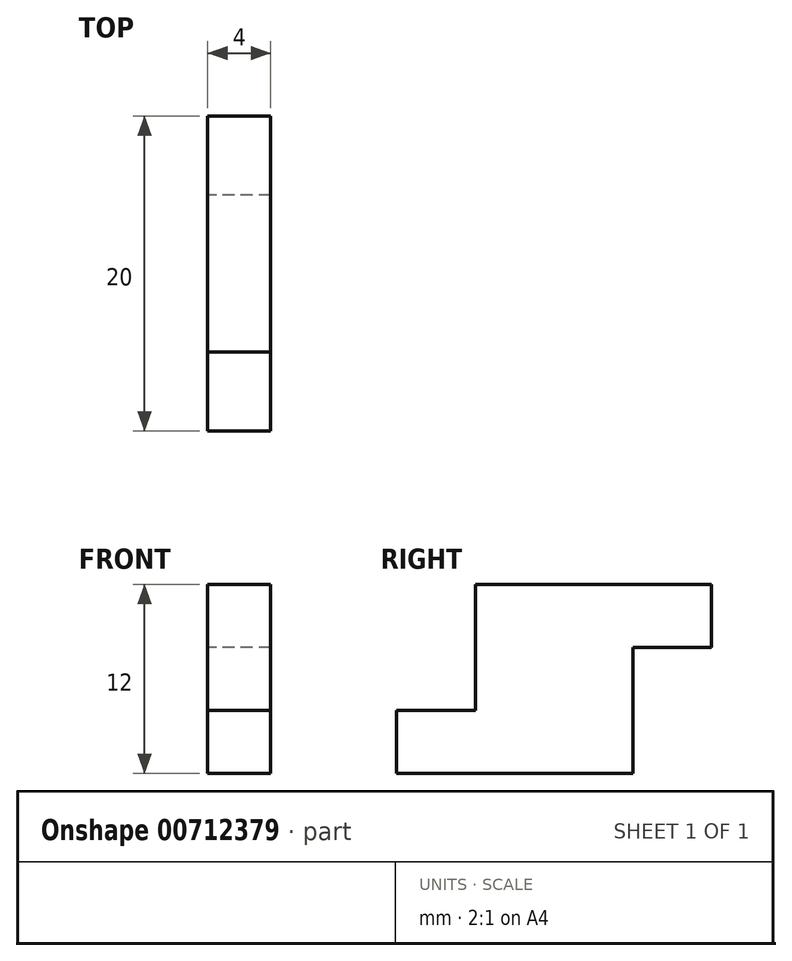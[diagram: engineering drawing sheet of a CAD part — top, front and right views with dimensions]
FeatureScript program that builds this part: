
annotation { "Feature Type Name" : "Feature", "Feature Type Description" : "" }
export const myFeature = defineFeature(function(context is Context, id is Id, definition is map)
    precondition{}
    {
        {
            var Q0;
            Q0=qCreatedBy(makeId("Right.planeOp"),FACE);
            var sketch = newSketch(context, id + "F0", { "sketchPlane" : qUnion([Q0])});
            skLineSegment(sketch, "E0", {"start": v(0, 0) * mm, "end": v(0, 8) * mm});
            skLineSegment(sketch, "E1", {"start": v(0, 8) * mm, "end": v(15, 8) * mm});
            skLineSegment(sketch, "E2", {"start": v(15, 8) * mm, "end": v(15, 4) * mm});
            skLineSegment(sketch, "E3", {"start": v(15, 4) * mm, "end": v(10, 4) * mm});
            skLineSegment(sketch, "E4", {"start": v(10, 4) * mm, "end": v(10, -4) * mm});
            skLineSegment(sketch, "E5", {"start": v(10, -4) * mm, "end": v(-5, -4) * mm});
            skLineSegment(sketch, "E6", {"start": v(-5, -4) * mm, "end": v(-5, 0) * mm});
            skLineSegment(sketch, "E7", {"start": v(-5, 0) * mm, "end": v(0, 0) * mm});
            skSolve(sketch);
        }
        {
            var Q0;
            Q0=makeQuery(id+"F0.imprint","IMPRINT",FACE,{"disambiguationData":[TD([[makeQuery(id+"F0.imprint","IMPRINT",EDGE,{"derivedFrom":sQuery(id+"F0.wireOp",EDGE,"E0")}),-1.0]])]});
            extrude(context, id + "F1", {"entities" : qUnion([Q0]), "depth" : 4 * mm, "offsetDistance" : 25 * mm});
        }
    });
